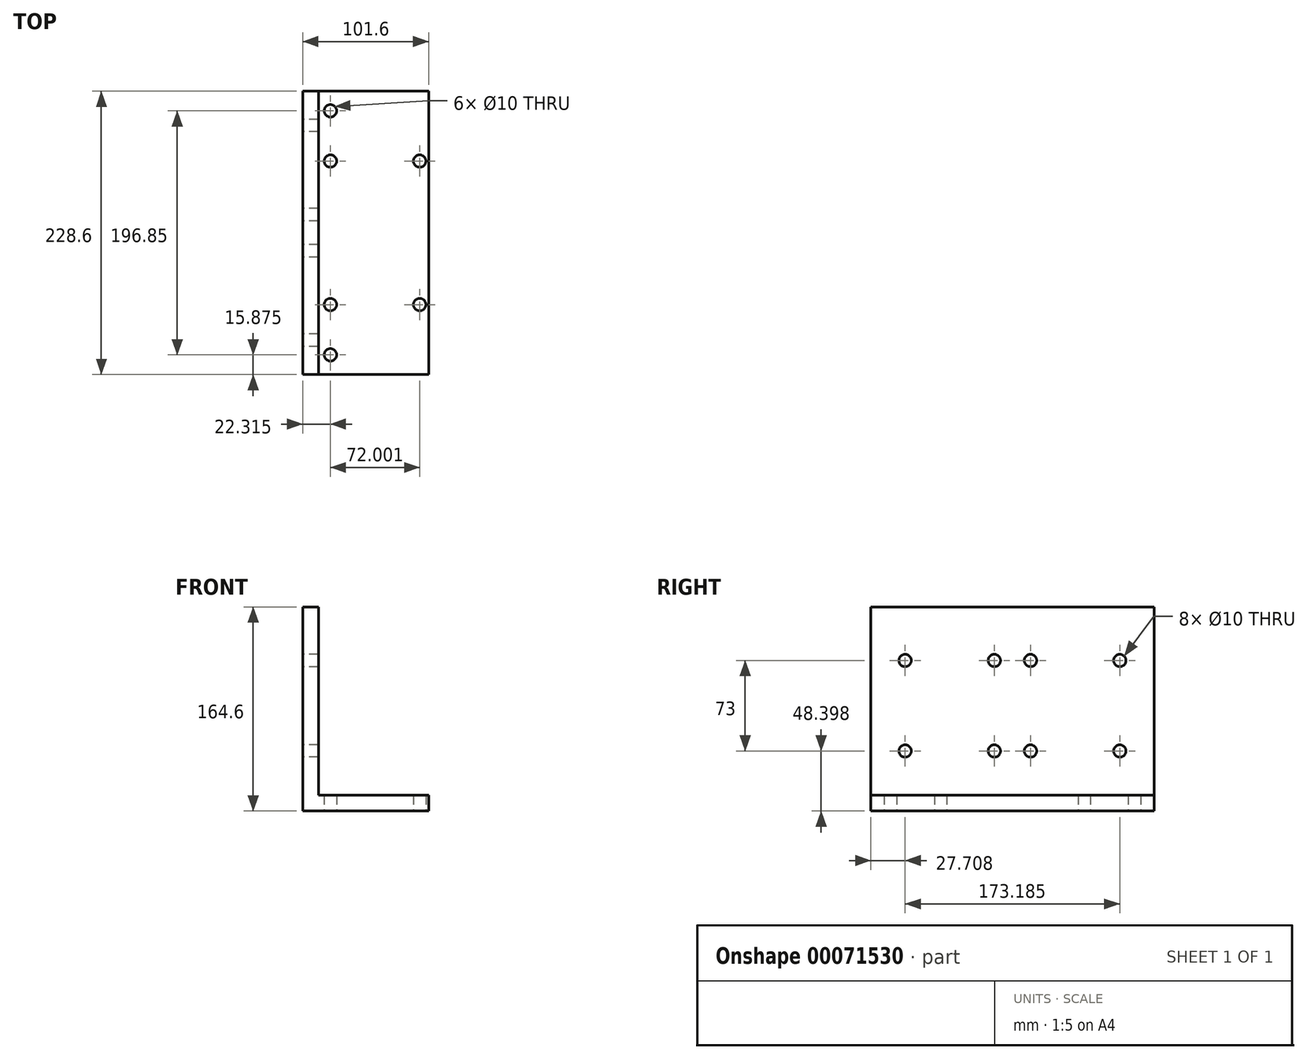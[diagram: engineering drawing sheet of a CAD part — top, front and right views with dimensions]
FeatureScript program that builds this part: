
annotation { "Feature Type Name" : "Feature", "Feature Type Description" : "" }
export const myFeature = defineFeature(function(context is Context, id is Id, definition is map)
    precondition{}
    {
        {
            var Q0;
            Q0=qCreatedBy(makeId("Front.planeOp"),FACE);
            var sketch = newSketch(context, id + "F0", { "sketchPlane" : qUnion([Q0])});
            skLineSegment(sketch, "E0.bottom", {"start": v(-97.33, 51.26) * mm, "end": v(-84.63, 51.26) * mm});
            skLineSegment(sketch, "E0.top", {"start": v(-97.33, -113.34) * mm, "end": v(4.27, -113.34) * mm});
            skLineSegment(sketch, "E0.left", {"start": v(-97.33, 51.26) * mm, "end": v(-97.33, -113.34) * mm});
            skLineSegment(sketch, "E0.right", {"start": v(4.27, -100.64) * mm, "end": v(4.27, -113.34) * mm});
            skLineSegment(sketch, "E1.top", {"start": v(4.27, -100.64) * mm, "end": v(-84.63, -100.64) * mm});
            skLineSegment(sketch, "E1.right", {"start": v(-84.63, 51.26) * mm, "end": v(-84.63, -100.64) * mm});
            skSolve(sketch);
        }
        {
            var Q0;
            Q0=qSketchRegion(id+"F0",true);
            extrude(context, id + "F1", {"entities" : qUnion([Q0]), "depth" : 228.6 * mm});
        }
        {
            var Q0;
            Q0=makeQuery(id+"F1.opExtrude","SWEPT_FACE",FACE,{"disambiguationData":[OSD([sQuery(id+"F0.wireOp",EDGE,"E0.top")])]});
            var sketch = newSketch(context, id + "F2", { "sketchPlane" : qUnion([Q0])});
            skCircle(sketch, "E2", {"center": v(-3.01, 172.2) * mm, "radius": 5 * mm});
            skCircle(sketch, "E3.0.1.0", {"center": v(-3.01, 56.4) * mm, "radius": 5 * mm});
            skCircle(sketch, "E3.1.0.0", {"center": v(-75.01, 172.2) * mm, "radius": 5 * mm});
            skCircle(sketch, "E3.1.1.0", {"center": v(-75.01, 56.4) * mm, "radius": 5 * mm});
            skLineSegment(sketch, "E3.direction1", {"start": v(-3.01, 172.2) * mm, "end": v(-75.01, 172.2) * mm, "construction": true});
            skLineSegment(sketch, "E3.direction2", {"start": v(-3.01, 172.2) * mm, "end": v(-3.01, 56.4) * mm, "construction": true});
            skCircle(sketch, "E4", {"center": v(-75.01, 15.88) * mm, "radius": 5 * mm});
            skCircle(sketch, "E5.0.1.0", {"center": v(-75.01, 212.73) * mm, "radius": 5 * mm});
            skLineSegment(sketch, "E5.direction1", {"start": v(-75.01, 15.88) * mm, "end": v(-3.01, 15.88) * mm, "construction": true});
            skLineSegment(sketch, "E5.direction2", {"start": v(-75.01, 15.88) * mm, "end": v(-75.01, 212.73) * mm, "construction": true});
            skSolve(sketch);
        }
        {
            var Q0;
            Q0=qSketchRegion(id+"F2",true);
            extrude(context, id + "F3", {"entities" : qUnion([Q0]), "operationType" : NewBodyOperationType.REMOVE, "oppositeDirection" : true, "depth" : 25 * mm});
        }
        {
            var Q0;
            Q0=makeQuery(id+"F1.opExtrude","SWEPT_FACE",FACE,{"disambiguationData":[OSD([sQuery(id+"F0.wireOp",EDGE,"E0.left")])]});
            var sketch = newSketch(context, id + "F4", { "sketchPlane" : qUnion([Q0])});
            skCircle(sketch, "E6", {"center": v(200.9, 8.06) * mm, "radius": 5 * mm});
            skCircle(sketch, "E7", {"center": v(128.9, 8.06) * mm, "radius": 5 * mm});
            skCircle(sketch, "E8", {"center": v(99.7, 8.06) * mm, "radius": 5 * mm});
            skCircle(sketch, "E9", {"center": v(27.7, 8.06) * mm, "radius": 5 * mm});
            skCircle(sketch, "E10", {"center": v(27.7, -64.94) * mm, "radius": 5 * mm});
            skCircle(sketch, "E11", {"center": v(99.7, -64.94) * mm, "radius": 5 * mm});
            skCircle(sketch, "E12", {"center": v(128.9, -64.94) * mm, "radius": 5 * mm});
            skCircle(sketch, "E13", {"center": v(200.9, -64.94) * mm, "radius": 5 * mm});
            skSolve(sketch);
        }
        {
            var Q0;
            Q0=qSketchRegion(id+"F4",true);
            extrude(context, id + "F5", {"entities" : qUnion([Q0]), "operationType" : NewBodyOperationType.REMOVE, "endBound" : BoundingType.THROUGH_ALL, "oppositeDirection" : true, "depth" : 25 * mm});
        }
    });
